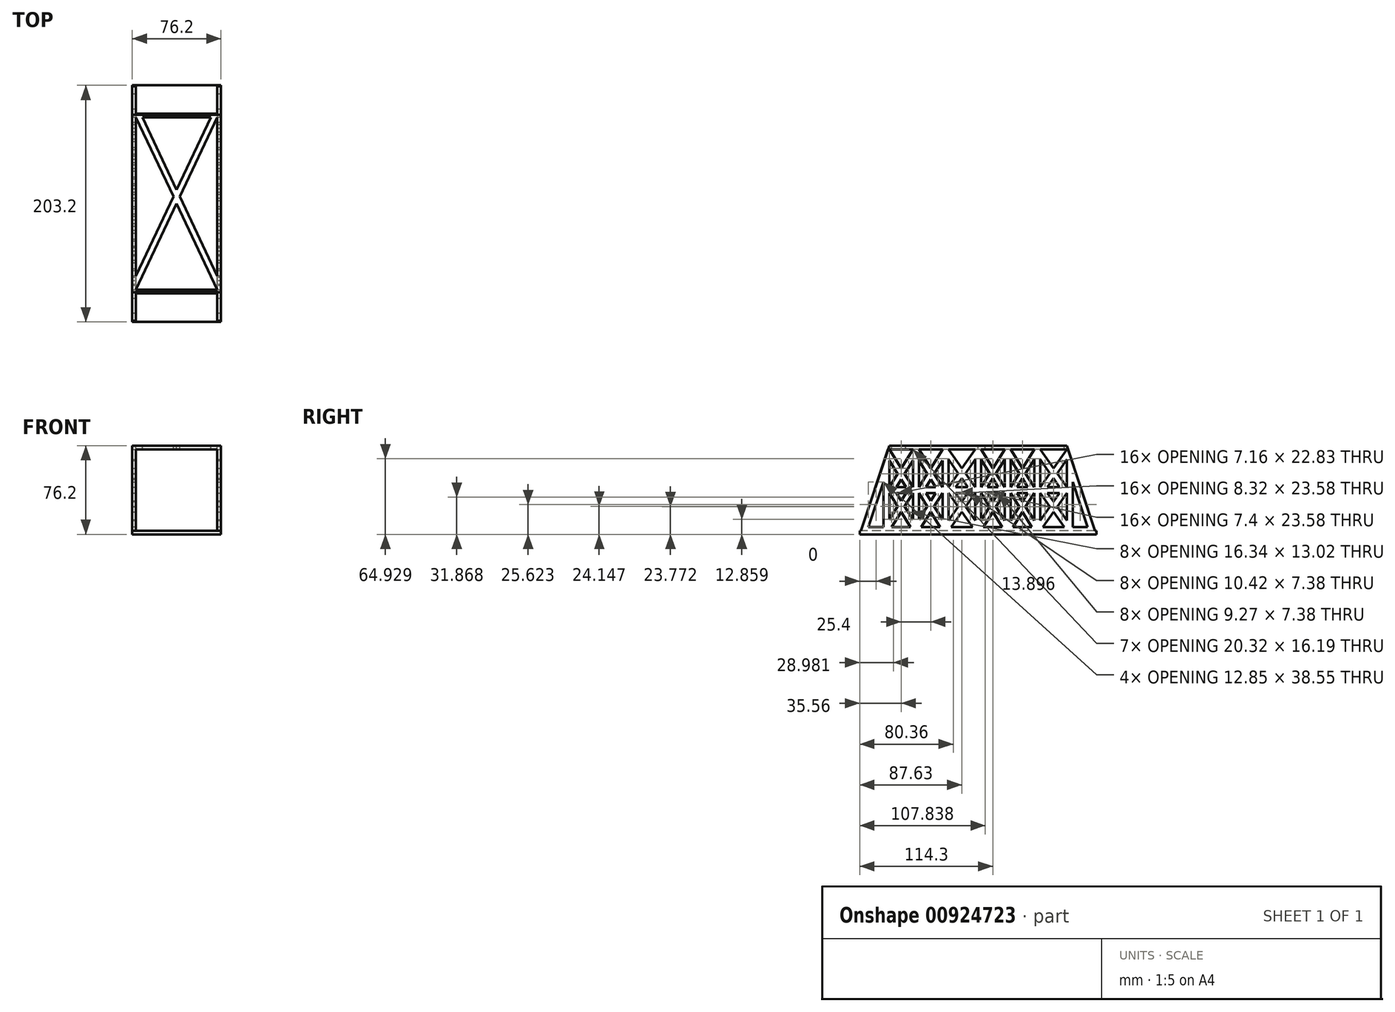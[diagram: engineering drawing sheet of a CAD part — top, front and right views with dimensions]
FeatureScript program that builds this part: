
annotation { "Feature Type Name" : "Feature", "Feature Type Description" : "" }
export const myFeature = defineFeature(function(context is Context, id is Id, definition is map)
    precondition{}
    {
        {
            var Q0;
            Q0=qCreatedBy(makeId("Right.planeOp"),FACE);
            var sketch = newSketch(context, id + "F0", { "sketchPlane" : qUnion([Q0])});
            skLineSegment(sketch, "E0", {"start": v(-101.6, -38.1) * mm, "end": v(101.6, -38.1) * mm});
            skLineSegment(sketch, "E1", {"start": v(-76.2, 38.1) * mm, "end": v(76.2, 38.1) * mm});
            skLineSegment(sketch, "E2", {"start": v(-76.2, 38.1) * mm, "end": v(-101.6, -38.1) * mm});
            skLineSegment(sketch, "E3", {"start": v(76.2, 38.1) * mm, "end": v(101.6, -38.1) * mm});
            skSolve(sketch);
        }
        {
            var Q0;
            Q0=qSketchRegion(id+"F0",true);
            extrude(context, id + "F1", {"entities" : qUnion([Q0]), "endBound" : BoundingType.SYMMETRIC, "depth" : 76.2 * mm, "offsetDistance" : 25.4 * mm});
        }
        {
            var Q0;
            Q0=makeQuery(id+"F1.opExtrude","CAP_FACE",FACE,{"disambiguationData":[OSD([sQuery(id+"F0.wireOp",EDGE,"E0"),sQuery(id+"F0.wireOp",EDGE,"E1"),sQuery(id+"F0.wireOp",EDGE,"E2"),sQuery(id+"F0.wireOp",EDGE,"E3")])],"isStart":false});
            var sketch = newSketch(context, id + "F2", { "sketchPlane" : qUnion([Q0])});
            skLineSegment(sketch, "E4.bottom", {"start": v(76.2, -34.93) * mm, "end": v(-76.2, -34.93) * mm});
            skLineSegment(sketch, "E4.top", {"start": v(76.2, 34.93) * mm, "end": v(-76.2, 34.93) * mm});
            skLineSegment(sketch, "E4.left", {"start": v(76.2, -34.93) * mm, "end": v(76.2, 34.93) * mm});
            skLineSegment(sketch, "E4.right", {"start": v(-76.2, -34.93) * mm, "end": v(-76.2, 34.93) * mm});
            skPoint(sketch, "E4.middle", {"position": v(0, 0) * mm});
            skLineSegment(sketch, "E5.bottom", {"start": v(76.2, -2.54) * mm, "end": v(-76.2, -2.54) * mm});
            skLineSegment(sketch, "E5.top", {"start": v(76.2, 2.54) * mm, "end": v(-76.2, 2.54) * mm});
            skLineSegment(sketch, "E5.left", {"start": v(76.2, -2.54) * mm, "end": v(76.2, 2.54) * mm});
            skLineSegment(sketch, "E5.right", {"start": v(-76.2, -2.54) * mm, "end": v(-76.2, 2.54) * mm});
            skLineSegment(sketch, "E6.bottom", {"start": v(-50.8, -34.93) * mm, "end": v(-55.88, -34.93) * mm});
            skLineSegment(sketch, "E6.top", {"start": v(-50.8, 34.93) * mm, "end": v(-55.88, 34.93) * mm});
            skLineSegment(sketch, "E6.left", {"start": v(-50.8, -34.92) * mm, "end": v(-50.8, 34.93) * mm});
            skLineSegment(sketch, "E6.right", {"start": v(-55.88, -34.92) * mm, "end": v(-55.88, 34.93) * mm});
            skPoint(sketch, "E6.middle", {"position": v(-53.34, 0) * mm});
            skLineSegment(sketch, "E7.bottom", {"start": v(-25.4, -34.93) * mm, "end": v(-30.48, -34.93) * mm});
            skLineSegment(sketch, "E7.top", {"start": v(-25.4, 34.93) * mm, "end": v(-30.48, 34.93) * mm});
            skLineSegment(sketch, "E7.left", {"start": v(-25.4, -34.93) * mm, "end": v(-25.4, 34.93) * mm});
            skLineSegment(sketch, "E7.right", {"start": v(-30.48, -34.93) * mm, "end": v(-30.48, 34.93) * mm});
            skPoint(sketch, "E7.middle", {"position": v(-27.94, 0) * mm});
            skLineSegment(sketch, "E8.bottom", {"start": v(27.94, -34.93) * mm, "end": v(22.86, -34.93) * mm});
            skLineSegment(sketch, "E8.top", {"start": v(27.94, 34.93) * mm, "end": v(22.86, 34.93) * mm});
            skLineSegment(sketch, "E8.left", {"start": v(27.94, -34.92) * mm, "end": v(27.94, 34.93) * mm});
            skLineSegment(sketch, "E8.right", {"start": v(22.86, -34.93) * mm, "end": v(22.86, 34.93) * mm});
            skPoint(sketch, "E8.middle", {"position": v(25.4, 0) * mm});
            skLineSegment(sketch, "E9.bottom", {"start": v(53.34, -34.93) * mm, "end": v(48.26, -34.93) * mm});
            skLineSegment(sketch, "E9.top", {"start": v(53.34, 34.93) * mm, "end": v(48.26, 34.93) * mm});
            skLineSegment(sketch, "E9.left", {"start": v(53.34, -34.93) * mm, "end": v(53.34, 34.93) * mm});
            skLineSegment(sketch, "E9.right", {"start": v(48.26, -34.93) * mm, "end": v(48.26, 34.93) * mm});
            skPoint(sketch, "E9.middle", {"position": v(50.8, 0) * mm});
            skLineSegment(sketch, "E10.bottom", {"start": v(2.54, -34.93) * mm, "end": v(-2.54, -34.93) * mm});
            skLineSegment(sketch, "E10.top", {"start": v(2.54, 34.93) * mm, "end": v(-2.54, 34.93) * mm});
            skLineSegment(sketch, "E10.left", {"start": v(2.54, -34.93) * mm, "end": v(2.54, 34.93) * mm});
            skLineSegment(sketch, "E10.right", {"start": v(-2.54, -34.93) * mm, "end": v(-2.54, 34.93) * mm});
            skLineSegment(sketch, "E11", {"start": v(-76.2, 34.93) * mm, "end": v(-55.88, 2.54) * mm});
            skLineSegment(sketch, "E12", {"start": v(-55.88, 34.93) * mm, "end": v(-76.2, 2.54) * mm});
            skLineSegment(sketch, "E13", {"start": v(-50.8, 34.93) * mm, "end": v(-30.48, 2.54) * mm});
            skLineSegment(sketch, "E14", {"start": v(-2.54, 34.92) * mm, "end": v(-25.4, 2.54) * mm});
            skLineSegment(sketch, "E15", {"start": v(-76.2, -2.54) * mm, "end": v(-55.88, -34.93) * mm});
            skLineSegment(sketch, "E16", {"start": v(-55.88, -2.54) * mm, "end": v(-76.2, -34.93) * mm});
            skLineSegment(sketch, "E17", {"start": v(-50.8, -2.54) * mm, "end": v(-30.48, -34.92) * mm});
            skLineSegment(sketch, "E18", {"start": v(-30.48, -2.54) * mm, "end": v(-50.8, -34.92) * mm});
            skLineSegment(sketch, "E19", {"start": v(-25.4, -2.54) * mm, "end": v(-2.54, -34.92) * mm});
            skLineSegment(sketch, "E20", {"start": v(-2.54, -2.54) * mm, "end": v(-25.4, -34.93) * mm});
            skLineSegment(sketch, "E21", {"start": v(-55.88, 25.37) * mm, "end": v(-70.2, 2.54) * mm});
            skLineSegment(sketch, "E22", {"start": v(-70.2, -2.54) * mm, "end": v(-55.88, -25.37) * mm});
            skLineSegment(sketch, "E23", {"start": v(-61.88, -2.54) * mm, "end": v(-76.2, -25.37) * mm});
            skLineSegment(sketch, "E24", {"start": v(-44.8, -2.54) * mm, "end": v(-30.48, -25.37) * mm});
            skLineSegment(sketch, "E25", {"start": v(-36.48, -2.54) * mm, "end": v(-50.8, -25.37) * mm});
            skLineSegment(sketch, "E26", {"start": v(-19.18, -2.54) * mm, "end": v(-2.54, -26.12) * mm});
            skLineSegment(sketch, "E27", {"start": v(-8.76, -2.54) * mm, "end": v(-25.4, -26.12) * mm});
            skLineSegment(sketch, "E28", {"start": v(-25.4, 34.93) * mm, "end": v(-2.54, 2.54) * mm});
            skLineSegment(sketch, "E29", {"start": v(-25.4, 26.12) * mm, "end": v(-8.76, 2.54) * mm});
            skLineSegment(sketch, "E30", {"start": v(-2.54, 26.12) * mm, "end": v(-19.18, 2.54) * mm});
            skLineSegment(sketch, "E31", {"start": v(-30.48, 34.92) * mm, "end": v(-50.8, 2.54) * mm});
            skLineSegment(sketch, "E32", {"start": v(-50.8, 25.37) * mm, "end": v(-36.48, 2.54) * mm});
            skLineSegment(sketch, "E33", {"start": v(-30.48, 25.37) * mm, "end": v(-44.8, 2.54) * mm});
            skLineSegment(sketch, "E34", {"start": v(-76.2, 25.37) * mm, "end": v(-61.88, 2.54) * mm});
            skLineSegment(sketch, "E35", {"start": v(2.54, 34.92) * mm, "end": v(22.86, 2.54) * mm});
            skLineSegment(sketch, "E36", {"start": v(22.86, 34.92) * mm, "end": v(2.54, 2.54) * mm});
            skLineSegment(sketch, "E37", {"start": v(2.54, 26.12) * mm, "end": v(17.33, 2.54) * mm});
            skLineSegment(sketch, "E38", {"start": v(22.86, 26.12) * mm, "end": v(8.07, 2.54) * mm});
            skLineSegment(sketch, "E39", {"start": v(27.94, 34.92) * mm, "end": v(48.26, 2.54) * mm});
            skLineSegment(sketch, "E40", {"start": v(27.94, 2.54) * mm, "end": v(48.26, 34.92) * mm});
            skLineSegment(sketch, "E41", {"start": v(53.34, 34.93) * mm, "end": v(76.2, 2.54) * mm});
            skLineSegment(sketch, "E42", {"start": v(53.34, 2.54) * mm, "end": v(76.2, 34.93) * mm});
            skLineSegment(sketch, "E43", {"start": v(53.34, -2.54) * mm, "end": v(76.2, -34.93) * mm});
            skLineSegment(sketch, "E44", {"start": v(53.34, -34.93) * mm, "end": v(76.2, -2.54) * mm});
            skLineSegment(sketch, "E45", {"start": v(48.26, -34.92) * mm, "end": v(27.94, -2.54) * mm});
            skLineSegment(sketch, "E46", {"start": v(48.26, -2.54) * mm, "end": v(27.94, -34.92) * mm});
            skLineSegment(sketch, "E47", {"start": v(2.54, -2.54) * mm, "end": v(22.86, -34.92) * mm});
            skLineSegment(sketch, "E48", {"start": v(22.86, -2.54) * mm, "end": v(2.54, -34.92) * mm});
            skLineSegment(sketch, "E49", {"start": v(27.94, 26.12) * mm, "end": v(42.73, 2.54) * mm});
            skLineSegment(sketch, "E50", {"start": v(48.26, 26.12) * mm, "end": v(33.47, 2.54) * mm});
            skLineSegment(sketch, "E51", {"start": v(53.34, 26.12) * mm, "end": v(69.98, 2.54) * mm});
            skLineSegment(sketch, "E52", {"start": v(76.2, 26.12) * mm, "end": v(59.56, 2.54) * mm});
            skLineSegment(sketch, "E53", {"start": v(59.56, -2.54) * mm, "end": v(76.2, -26.12) * mm});
            skLineSegment(sketch, "E54", {"start": v(69.98, -2.54) * mm, "end": v(53.34, -26.12) * mm});
            skLineSegment(sketch, "E55", {"start": v(48.26, -26.12) * mm, "end": v(33.47, -2.54) * mm});
            skLineSegment(sketch, "E56", {"start": v(42.73, -2.54) * mm, "end": v(27.94, -26.12) * mm});
            skLineSegment(sketch, "E57", {"start": v(22.86, -26.12) * mm, "end": v(8.07, -2.54) * mm});
            skLineSegment(sketch, "E58", {"start": v(17.33, -2.54) * mm, "end": v(2.54, -26.12) * mm});
            skLineSegment(sketch, "E59", {"start": v(-81.28, -34.93) * mm, "end": v(-81.28, 6.8) * mm});
            skLineSegment(sketch, "E60", {"start": v(-81.28, 6.8) * mm, "end": v(-95.19, -34.93) * mm});
            skLineSegment(sketch, "E61", {"start": v(-95.19, -34.92) * mm, "end": v(-81.28, -34.93) * mm});
            skLineSegment(sketch, "E62.MirrorCS", {"start": v(81.28, 6.8) * mm, "end": v(95.19, -34.93) * mm});
            skLineSegment(sketch, "E63.MirrorCS", {"start": v(81.28, -34.93) * mm, "end": v(81.28, 6.8) * mm});
            skLineSegment(sketch, "E64.MirrorCS", {"start": v(95.19, -34.92) * mm, "end": v(81.28, -34.93) * mm});
            skSolve(sketch);
        }
        {
            var Q0;
            Q0=makeQuery(id+"F2.imprint","IMPRINT",FACE,{"disambiguationData":[TD([[makeQuery(id+"F2.imprint","IMPRINT",EDGE,{"derivedFrom":sQuery(id+"F2.wireOp",EDGE,"E59")}),1.0]])]});
            var Q1;
            {var subQ0=sQuery(id+"F2.wireOp",EDGE,"E16");var subQ3=sQuery(id+"F2.wireOp",EDGE,"E15");var subQ5=makeQuery(id+"F2.imprint","INTERSECT",VERTEX,{"derivedFrom":[subQ3,subQ0]});Q1=makeQuery(id+"F2.imprint","IMPRINT",FACE,{"disambiguationData":[TD([[makeQuery(id+"F2.imprint","IMPRINT",EDGE,{"disambiguationData":[TD([[subQ5,-1.0]])],"derivedFrom":subQ0}),1.0]])]});}
            var Q2;
            {var subQ1=sQuery(id+"F2.wireOp",EDGE,"E4.right");var subQ3=sQuery(id+"F2.wireOp",EDGE,"E23");var subQ4=makeQuery(id+"F2.imprint","INTERSECT",VERTEX,{"derivedFrom":[subQ1,subQ3]});Q2=makeQuery(id+"F2.imprint","IMPRINT",FACE,{"disambiguationData":[TD([[makeQuery(id+"F2.imprint","IMPRINT",EDGE,{"disambiguationData":[TD([[subQ4,1.0]])],"derivedFrom":subQ3}),-1.0]])]});}
            var Q3;
            {var subQ0=sQuery(id+"F2.wireOp",EDGE,"E22");var subQ1=sQuery(id+"F2.wireOp",EDGE,"E5.bottom");var subQ2=makeQuery(id+"F2.imprint","INTERSECT",VERTEX,{"derivedFrom":[subQ1,subQ0]});Q3=makeQuery(id+"F2.imprint","IMPRINT",FACE,{"disambiguationData":[TD([[makeQuery(id+"F2.imprint","IMPRINT",EDGE,{"disambiguationData":[TD([[subQ2,1.0]])],"derivedFrom":subQ1}),1.0]])]});}
            var Q4;
            {var subQ1=sQuery(id+"F2.wireOp",EDGE,"E6.right");var subQ3=sQuery(id+"F2.wireOp",EDGE,"E22");var subQ4=makeQuery(id+"F2.imprint","INTERSECT",VERTEX,{"derivedFrom":[subQ1,subQ3]});Q4=makeQuery(id+"F2.imprint","IMPRINT",FACE,{"disambiguationData":[TD([[makeQuery(id+"F2.imprint","IMPRINT",EDGE,{"disambiguationData":[TD([[subQ4,1.0]])],"derivedFrom":subQ3}),1.0]])]});}
            var Q5;
            {var subQ0=sQuery(id+"F2.wireOp",EDGE,"E21");var subQ1=sQuery(id+"F2.wireOp",EDGE,"E5.top");var subQ2=makeQuery(id+"F2.imprint","INTERSECT",VERTEX,{"derivedFrom":[subQ1,subQ0]});Q5=makeQuery(id+"F2.imprint","IMPRINT",FACE,{"disambiguationData":[TD([[makeQuery(id+"F2.imprint","IMPRINT",EDGE,{"disambiguationData":[TD([[subQ2,1.0]])],"derivedFrom":subQ1}),-1.0]])]});}
            var Q6;
            {var subQ0=sQuery(id+"F2.wireOp",EDGE,"E11");var subQ3=sQuery(id+"F2.wireOp",EDGE,"E12");var subQ5=makeQuery(id+"F2.imprint","INTERSECT",VERTEX,{"derivedFrom":[subQ0,subQ3]});Q6=makeQuery(id+"F2.imprint","IMPRINT",FACE,{"disambiguationData":[TD([[makeQuery(id+"F2.imprint","IMPRINT",EDGE,{"disambiguationData":[TD([[subQ5,1.0]])],"derivedFrom":subQ0}),1.0]])]});}
            var Q7;
            {var subQ1=sQuery(id+"F2.wireOp",EDGE,"E4.right");var subQ3=sQuery(id+"F2.wireOp",EDGE,"E34");var subQ4=makeQuery(id+"F2.imprint","INTERSECT",VERTEX,{"derivedFrom":[subQ1,subQ3]});Q7=makeQuery(id+"F2.imprint","IMPRINT",FACE,{"disambiguationData":[TD([[makeQuery(id+"F2.imprint","IMPRINT",EDGE,{"disambiguationData":[TD([[subQ4,-1.0]])],"derivedFrom":subQ3}),-1.0]])]});}
            var Q8;
            {var subQ1=sQuery(id+"F2.wireOp",EDGE,"E6.right");var subQ3=sQuery(id+"F2.wireOp",EDGE,"E21");var subQ4=makeQuery(id+"F2.imprint","INTERSECT",VERTEX,{"derivedFrom":[subQ1,subQ3]});Q8=makeQuery(id+"F2.imprint","IMPRINT",FACE,{"disambiguationData":[TD([[makeQuery(id+"F2.imprint","IMPRINT",EDGE,{"disambiguationData":[TD([[subQ4,-1.0]])],"derivedFrom":subQ3}),1.0]])]});}
            var Q9;
            {var subQ0=sQuery(id+"F2.wireOp",EDGE,"E13");var subQ3=sQuery(id+"F2.wireOp",EDGE,"E31");var subQ5=makeQuery(id+"F2.imprint","INTERSECT",VERTEX,{"derivedFrom":[subQ0,subQ3]});Q9=makeQuery(id+"F2.imprint","IMPRINT",FACE,{"disambiguationData":[TD([[makeQuery(id+"F2.imprint","IMPRINT",EDGE,{"disambiguationData":[TD([[subQ5,1.0]])],"derivedFrom":subQ0}),1.0]])]});}
            var Q10;
            {var subQ1=sQuery(id+"F2.wireOp",EDGE,"E6.left");var subQ3=sQuery(id+"F2.wireOp",EDGE,"E32");var subQ4=makeQuery(id+"F2.imprint","INTERSECT",VERTEX,{"derivedFrom":[subQ1,subQ3]});Q10=makeQuery(id+"F2.imprint","IMPRINT",FACE,{"disambiguationData":[TD([[makeQuery(id+"F2.imprint","IMPRINT",EDGE,{"disambiguationData":[TD([[subQ4,-1.0]])],"derivedFrom":subQ3}),-1.0]])]});}
            var Q11;
            {var subQ1=sQuery(id+"F2.wireOp",EDGE,"E7.right");var subQ3=sQuery(id+"F2.wireOp",EDGE,"E33");var subQ4=makeQuery(id+"F2.imprint","INTERSECT",VERTEX,{"derivedFrom":[subQ1,subQ3]});Q11=makeQuery(id+"F2.imprint","IMPRINT",FACE,{"disambiguationData":[TD([[makeQuery(id+"F2.imprint","IMPRINT",EDGE,{"disambiguationData":[TD([[subQ4,-1.0]])],"derivedFrom":subQ3}),1.0]])]});}
            var Q12;
            {var subQ0=sQuery(id+"F2.wireOp",EDGE,"E32");var subQ1=sQuery(id+"F2.wireOp",EDGE,"E5.top");var subQ2=makeQuery(id+"F2.imprint","INTERSECT",VERTEX,{"derivedFrom":[subQ1,subQ0]});Q12=makeQuery(id+"F2.imprint","IMPRINT",FACE,{"disambiguationData":[TD([[makeQuery(id+"F2.imprint","IMPRINT",EDGE,{"disambiguationData":[TD([[subQ2,-1.0]])],"derivedFrom":subQ1}),-1.0]])]});}
            var Q13;
            {var subQ0=sQuery(id+"F2.wireOp",EDGE,"E24");var subQ1=sQuery(id+"F2.wireOp",EDGE,"E5.bottom");var subQ2=makeQuery(id+"F2.imprint","INTERSECT",VERTEX,{"derivedFrom":[subQ1,subQ0]});Q13=makeQuery(id+"F2.imprint","IMPRINT",FACE,{"disambiguationData":[TD([[makeQuery(id+"F2.imprint","IMPRINT",EDGE,{"disambiguationData":[TD([[subQ2,1.0]])],"derivedFrom":subQ1}),1.0]])]});}
            var Q14;
            {var subQ1=sQuery(id+"F2.wireOp",EDGE,"E6.left");var subQ3=sQuery(id+"F2.wireOp",EDGE,"E25");var subQ4=makeQuery(id+"F2.imprint","INTERSECT",VERTEX,{"derivedFrom":[subQ1,subQ3]});Q14=makeQuery(id+"F2.imprint","IMPRINT",FACE,{"disambiguationData":[TD([[makeQuery(id+"F2.imprint","IMPRINT",EDGE,{"disambiguationData":[TD([[subQ4,1.0]])],"derivedFrom":subQ3}),-1.0]])]});}
            var Q15;
            {var subQ1=sQuery(id+"F2.wireOp",EDGE,"E7.right");var subQ3=sQuery(id+"F2.wireOp",EDGE,"E24");var subQ4=makeQuery(id+"F2.imprint","INTERSECT",VERTEX,{"derivedFrom":[subQ1,subQ3]});Q15=makeQuery(id+"F2.imprint","IMPRINT",FACE,{"disambiguationData":[TD([[makeQuery(id+"F2.imprint","IMPRINT",EDGE,{"disambiguationData":[TD([[subQ4,1.0]])],"derivedFrom":subQ3}),1.0]])]});}
            var Q16;
            {var subQ0=sQuery(id+"F2.wireOp",EDGE,"E18");var subQ3=sQuery(id+"F2.wireOp",EDGE,"E17");var subQ5=makeQuery(id+"F2.imprint","INTERSECT",VERTEX,{"derivedFrom":[subQ3,subQ0]});Q16=makeQuery(id+"F2.imprint","IMPRINT",FACE,{"disambiguationData":[TD([[makeQuery(id+"F2.imprint","IMPRINT",EDGE,{"disambiguationData":[TD([[subQ5,-1.0]])],"derivedFrom":subQ3}),-1.0]])]});}
            var Q17;
            {var subQ1=sQuery(id+"F2.wireOp",EDGE,"E7.left");var subQ3=sQuery(id+"F2.wireOp",EDGE,"E29");var subQ4=makeQuery(id+"F2.imprint","INTERSECT",VERTEX,{"derivedFrom":[subQ1,subQ3]});Q17=makeQuery(id+"F2.imprint","IMPRINT",FACE,{"disambiguationData":[TD([[makeQuery(id+"F2.imprint","IMPRINT",EDGE,{"disambiguationData":[TD([[subQ4,-1.0]])],"derivedFrom":subQ3}),-1.0]])]});}
            var Q18;
            {var subQ0=sQuery(id+"F2.wireOp",EDGE,"E28");var subQ3=sQuery(id+"F2.wireOp",EDGE,"E14");var subQ5=makeQuery(id+"F2.imprint","INTERSECT",VERTEX,{"derivedFrom":[subQ3,subQ0]});Q18=makeQuery(id+"F2.imprint","IMPRINT",FACE,{"disambiguationData":[TD([[makeQuery(id+"F2.imprint","IMPRINT",EDGE,{"disambiguationData":[TD([[subQ5,1.0]])],"derivedFrom":subQ3}),-1.0]])]});}
            var Q19;
            {var subQ1=sQuery(id+"F2.wireOp",EDGE,"E10.right");var subQ3=sQuery(id+"F2.wireOp",EDGE,"E30");var subQ4=makeQuery(id+"F2.imprint","INTERSECT",VERTEX,{"derivedFrom":[subQ1,subQ3]});Q19=makeQuery(id+"F2.imprint","IMPRINT",FACE,{"disambiguationData":[TD([[makeQuery(id+"F2.imprint","IMPRINT",EDGE,{"disambiguationData":[TD([[subQ4,-1.0]])],"derivedFrom":subQ3}),1.0]])]});}
            var Q20;
            {var subQ0=sQuery(id+"F2.wireOp",EDGE,"E29");var subQ1=sQuery(id+"F2.wireOp",EDGE,"E5.top");var subQ2=makeQuery(id+"F2.imprint","INTERSECT",VERTEX,{"derivedFrom":[subQ1,subQ0]});Q20=makeQuery(id+"F2.imprint","IMPRINT",FACE,{"disambiguationData":[TD([[makeQuery(id+"F2.imprint","IMPRINT",EDGE,{"disambiguationData":[TD([[subQ2,-1.0]])],"derivedFrom":subQ1}),-1.0]])]});}
            var Q21;
            {var subQ0=sQuery(id+"F2.wireOp",EDGE,"E26");var subQ1=sQuery(id+"F2.wireOp",EDGE,"E5.bottom");var subQ2=makeQuery(id+"F2.imprint","INTERSECT",VERTEX,{"derivedFrom":[subQ1,subQ0]});Q21=makeQuery(id+"F2.imprint","IMPRINT",FACE,{"disambiguationData":[TD([[makeQuery(id+"F2.imprint","IMPRINT",EDGE,{"disambiguationData":[TD([[subQ2,1.0]])],"derivedFrom":subQ1}),1.0]])]});}
            var Q22;
            {var subQ1=sQuery(id+"F2.wireOp",EDGE,"E7.left");var subQ3=sQuery(id+"F2.wireOp",EDGE,"E27");var subQ4=makeQuery(id+"F2.imprint","INTERSECT",VERTEX,{"derivedFrom":[subQ1,subQ3]});Q22=makeQuery(id+"F2.imprint","IMPRINT",FACE,{"disambiguationData":[TD([[makeQuery(id+"F2.imprint","IMPRINT",EDGE,{"disambiguationData":[TD([[subQ4,1.0]])],"derivedFrom":subQ3}),-1.0]])]});}
            var Q23;
            {var subQ1=sQuery(id+"F2.wireOp",EDGE,"E10.right");var subQ3=sQuery(id+"F2.wireOp",EDGE,"E26");var subQ4=makeQuery(id+"F2.imprint","INTERSECT",VERTEX,{"derivedFrom":[subQ1,subQ3]});Q23=makeQuery(id+"F2.imprint","IMPRINT",FACE,{"disambiguationData":[TD([[makeQuery(id+"F2.imprint","IMPRINT",EDGE,{"disambiguationData":[TD([[subQ4,1.0]])],"derivedFrom":subQ3}),1.0]])]});}
            var Q24;
            {var subQ0=sQuery(id+"F2.wireOp",EDGE,"E20");var subQ3=sQuery(id+"F2.wireOp",EDGE,"E19");var subQ5=makeQuery(id+"F2.imprint","INTERSECT",VERTEX,{"derivedFrom":[subQ3,subQ0]});Q24=makeQuery(id+"F2.imprint","IMPRINT",FACE,{"disambiguationData":[TD([[makeQuery(id+"F2.imprint","IMPRINT",EDGE,{"disambiguationData":[TD([[subQ5,-1.0]])],"derivedFrom":subQ3}),-1.0]])]});}
            var Q25;
            {var subQ1=sQuery(id+"F2.wireOp",EDGE,"E10.left");var subQ3=sQuery(id+"F2.wireOp",EDGE,"E37");var subQ4=makeQuery(id+"F2.imprint","INTERSECT",VERTEX,{"derivedFrom":[subQ1,subQ3]});Q25=makeQuery(id+"F2.imprint","IMPRINT",FACE,{"disambiguationData":[TD([[makeQuery(id+"F2.imprint","IMPRINT",EDGE,{"disambiguationData":[TD([[subQ4,-1.0]])],"derivedFrom":subQ3}),-1.0]])]});}
            var Q26;
            {var subQ0=sQuery(id+"F2.wireOp",EDGE,"E36");var subQ3=sQuery(id+"F2.wireOp",EDGE,"E35");var subQ5=makeQuery(id+"F2.imprint","INTERSECT",VERTEX,{"derivedFrom":[subQ3,subQ0]});Q26=makeQuery(id+"F2.imprint","IMPRINT",FACE,{"disambiguationData":[TD([[makeQuery(id+"F2.imprint","IMPRINT",EDGE,{"disambiguationData":[TD([[subQ5,1.0]])],"derivedFrom":subQ3}),1.0]])]});}
            var Q27;
            {var subQ1=sQuery(id+"F2.wireOp",EDGE,"E8.right");var subQ3=sQuery(id+"F2.wireOp",EDGE,"E38");var subQ4=makeQuery(id+"F2.imprint","INTERSECT",VERTEX,{"derivedFrom":[subQ1,subQ3]});Q27=makeQuery(id+"F2.imprint","IMPRINT",FACE,{"disambiguationData":[TD([[makeQuery(id+"F2.imprint","IMPRINT",EDGE,{"disambiguationData":[TD([[subQ4,-1.0]])],"derivedFrom":subQ3}),1.0]])]});}
            var Q28;
            {var subQ0=sQuery(id+"F2.wireOp",EDGE,"E37");var subQ1=sQuery(id+"F2.wireOp",EDGE,"E5.top");var subQ2=makeQuery(id+"F2.imprint","INTERSECT",VERTEX,{"derivedFrom":[subQ1,subQ0]});Q28=makeQuery(id+"F2.imprint","IMPRINT",FACE,{"disambiguationData":[TD([[makeQuery(id+"F2.imprint","IMPRINT",EDGE,{"disambiguationData":[TD([[subQ2,-1.0]])],"derivedFrom":subQ1}),-1.0]])]});}
            var Q29;
            {var subQ0=sQuery(id+"F2.wireOp",EDGE,"E57");var subQ1=sQuery(id+"F2.wireOp",EDGE,"E5.bottom");var subQ2=makeQuery(id+"F2.imprint","INTERSECT",VERTEX,{"derivedFrom":[subQ1,subQ0]});Q29=makeQuery(id+"F2.imprint","IMPRINT",FACE,{"disambiguationData":[TD([[makeQuery(id+"F2.imprint","IMPRINT",EDGE,{"disambiguationData":[TD([[subQ2,1.0]])],"derivedFrom":subQ1}),1.0]])]});}
            var Q30;
            {var subQ1=sQuery(id+"F2.wireOp",EDGE,"E10.left");var subQ3=sQuery(id+"F2.wireOp",EDGE,"E58");var subQ4=makeQuery(id+"F2.imprint","INTERSECT",VERTEX,{"derivedFrom":[subQ1,subQ3]});Q30=makeQuery(id+"F2.imprint","IMPRINT",FACE,{"disambiguationData":[TD([[makeQuery(id+"F2.imprint","IMPRINT",EDGE,{"disambiguationData":[TD([[subQ4,1.0]])],"derivedFrom":subQ3}),-1.0]])]});}
            var Q31;
            {var subQ1=sQuery(id+"F2.wireOp",EDGE,"E8.right");var subQ3=sQuery(id+"F2.wireOp",EDGE,"E57");var subQ4=makeQuery(id+"F2.imprint","INTERSECT",VERTEX,{"derivedFrom":[subQ1,subQ3]});Q31=makeQuery(id+"F2.imprint","IMPRINT",FACE,{"disambiguationData":[TD([[makeQuery(id+"F2.imprint","IMPRINT",EDGE,{"disambiguationData":[TD([[subQ4,-1.0]])],"derivedFrom":subQ3}),-1.0]])]});}
            var Q32;
            {var subQ0=sQuery(id+"F2.wireOp",EDGE,"E47");var subQ3=sQuery(id+"F2.wireOp",EDGE,"E48");var subQ5=makeQuery(id+"F2.imprint","INTERSECT",VERTEX,{"derivedFrom":[subQ0,subQ3]});Q32=makeQuery(id+"F2.imprint","IMPRINT",FACE,{"disambiguationData":[TD([[makeQuery(id+"F2.imprint","IMPRINT",EDGE,{"disambiguationData":[TD([[subQ5,-1.0]])],"derivedFrom":subQ0}),-1.0]])]});}
            var Q33;
            {var subQ1=sQuery(id+"F2.wireOp",EDGE,"E8.left");var subQ3=sQuery(id+"F2.wireOp",EDGE,"E49");var subQ4=makeQuery(id+"F2.imprint","INTERSECT",VERTEX,{"derivedFrom":[subQ1,subQ3]});Q33=makeQuery(id+"F2.imprint","IMPRINT",FACE,{"disambiguationData":[TD([[makeQuery(id+"F2.imprint","IMPRINT",EDGE,{"disambiguationData":[TD([[subQ4,-1.0]])],"derivedFrom":subQ3}),-1.0]])]});}
            var Q34;
            {var subQ0=sQuery(id+"F2.wireOp",EDGE,"E39");var subQ3=sQuery(id+"F2.wireOp",EDGE,"E40");var subQ5=makeQuery(id+"F2.imprint","INTERSECT",VERTEX,{"derivedFrom":[subQ0,subQ3]});Q34=makeQuery(id+"F2.imprint","IMPRINT",FACE,{"disambiguationData":[TD([[makeQuery(id+"F2.imprint","IMPRINT",EDGE,{"disambiguationData":[TD([[subQ5,1.0]])],"derivedFrom":subQ0}),1.0]])]});}
            var Q35;
            {var subQ1=sQuery(id+"F2.wireOp",EDGE,"E9.right");var subQ3=sQuery(id+"F2.wireOp",EDGE,"E50");var subQ4=makeQuery(id+"F2.imprint","INTERSECT",VERTEX,{"derivedFrom":[subQ1,subQ3]});Q35=makeQuery(id+"F2.imprint","IMPRINT",FACE,{"disambiguationData":[TD([[makeQuery(id+"F2.imprint","IMPRINT",EDGE,{"disambiguationData":[TD([[subQ4,-1.0]])],"derivedFrom":subQ3}),1.0]])]});}
            var Q36;
            {var subQ0=sQuery(id+"F2.wireOp",EDGE,"E49");var subQ1=sQuery(id+"F2.wireOp",EDGE,"E5.top");var subQ2=makeQuery(id+"F2.imprint","INTERSECT",VERTEX,{"derivedFrom":[subQ1,subQ0]});Q36=makeQuery(id+"F2.imprint","IMPRINT",FACE,{"disambiguationData":[TD([[makeQuery(id+"F2.imprint","IMPRINT",EDGE,{"disambiguationData":[TD([[subQ2,-1.0]])],"derivedFrom":subQ1}),-1.0]])]});}
            var Q37;
            {var subQ0=sQuery(id+"F2.wireOp",EDGE,"E55");var subQ1=sQuery(id+"F2.wireOp",EDGE,"E5.bottom");var subQ2=makeQuery(id+"F2.imprint","INTERSECT",VERTEX,{"derivedFrom":[subQ1,subQ0]});Q37=makeQuery(id+"F2.imprint","IMPRINT",FACE,{"disambiguationData":[TD([[makeQuery(id+"F2.imprint","IMPRINT",EDGE,{"disambiguationData":[TD([[subQ2,1.0]])],"derivedFrom":subQ1}),1.0]])]});}
            var Q38;
            {var subQ1=sQuery(id+"F2.wireOp",EDGE,"E8.left");var subQ3=sQuery(id+"F2.wireOp",EDGE,"E56");var subQ4=makeQuery(id+"F2.imprint","INTERSECT",VERTEX,{"derivedFrom":[subQ1,subQ3]});Q38=makeQuery(id+"F2.imprint","IMPRINT",FACE,{"disambiguationData":[TD([[makeQuery(id+"F2.imprint","IMPRINT",EDGE,{"disambiguationData":[TD([[subQ4,1.0]])],"derivedFrom":subQ3}),-1.0]])]});}
            var Q39;
            {var subQ1=sQuery(id+"F2.wireOp",EDGE,"E9.right");var subQ3=sQuery(id+"F2.wireOp",EDGE,"E55");var subQ4=makeQuery(id+"F2.imprint","INTERSECT",VERTEX,{"derivedFrom":[subQ1,subQ3]});Q39=makeQuery(id+"F2.imprint","IMPRINT",FACE,{"disambiguationData":[TD([[makeQuery(id+"F2.imprint","IMPRINT",EDGE,{"disambiguationData":[TD([[subQ4,-1.0]])],"derivedFrom":subQ3}),-1.0]])]});}
            var Q40;
            {var subQ0=sQuery(id+"F2.wireOp",EDGE,"E46");var subQ3=sQuery(id+"F2.wireOp",EDGE,"E45");var subQ5=makeQuery(id+"F2.imprint","INTERSECT",VERTEX,{"derivedFrom":[subQ3,subQ0]});Q40=makeQuery(id+"F2.imprint","IMPRINT",FACE,{"disambiguationData":[TD([[makeQuery(id+"F2.imprint","IMPRINT",EDGE,{"disambiguationData":[TD([[subQ5,1.0]])],"derivedFrom":subQ3}),1.0]])]});}
            var Q41;
            {var subQ1=sQuery(id+"F2.wireOp",EDGE,"E9.left");var subQ3=sQuery(id+"F2.wireOp",EDGE,"E51");var subQ4=makeQuery(id+"F2.imprint","INTERSECT",VERTEX,{"derivedFrom":[subQ1,subQ3]});Q41=makeQuery(id+"F2.imprint","IMPRINT",FACE,{"disambiguationData":[TD([[makeQuery(id+"F2.imprint","IMPRINT",EDGE,{"disambiguationData":[TD([[subQ4,-1.0]])],"derivedFrom":subQ3}),-1.0]])]});}
            var Q42;
            {var subQ0=sQuery(id+"F2.wireOp",EDGE,"E42");var subQ3=sQuery(id+"F2.wireOp",EDGE,"E41");var subQ5=makeQuery(id+"F2.imprint","INTERSECT",VERTEX,{"derivedFrom":[subQ3,subQ0]});Q42=makeQuery(id+"F2.imprint","IMPRINT",FACE,{"disambiguationData":[TD([[makeQuery(id+"F2.imprint","IMPRINT",EDGE,{"disambiguationData":[TD([[subQ5,-1.0]])],"derivedFrom":subQ0}),1.0]])]});}
            var Q43;
            {var subQ1=sQuery(id+"F2.wireOp",EDGE,"E4.left");var subQ3=sQuery(id+"F2.wireOp",EDGE,"E52");var subQ4=makeQuery(id+"F2.imprint","INTERSECT",VERTEX,{"derivedFrom":[subQ1,subQ3]});Q43=makeQuery(id+"F2.imprint","IMPRINT",FACE,{"disambiguationData":[TD([[makeQuery(id+"F2.imprint","IMPRINT",EDGE,{"disambiguationData":[TD([[subQ4,-1.0]])],"derivedFrom":subQ3}),1.0]])]});}
            var Q44;
            {var subQ0=sQuery(id+"F2.wireOp",EDGE,"E51");var subQ1=sQuery(id+"F2.wireOp",EDGE,"E5.top");var subQ2=makeQuery(id+"F2.imprint","INTERSECT",VERTEX,{"derivedFrom":[subQ1,subQ0]});Q44=makeQuery(id+"F2.imprint","IMPRINT",FACE,{"disambiguationData":[TD([[makeQuery(id+"F2.imprint","IMPRINT",EDGE,{"disambiguationData":[TD([[subQ2,-1.0]])],"derivedFrom":subQ1}),-1.0]])]});}
            var Q45;
            {var subQ0=sQuery(id+"F2.wireOp",EDGE,"E53");var subQ1=sQuery(id+"F2.wireOp",EDGE,"E5.bottom");var subQ2=makeQuery(id+"F2.imprint","INTERSECT",VERTEX,{"derivedFrom":[subQ1,subQ0]});Q45=makeQuery(id+"F2.imprint","IMPRINT",FACE,{"disambiguationData":[TD([[makeQuery(id+"F2.imprint","IMPRINT",EDGE,{"disambiguationData":[TD([[subQ2,1.0]])],"derivedFrom":subQ1}),1.0]])]});}
            var Q46;
            {var subQ1=sQuery(id+"F2.wireOp",EDGE,"E9.left");var subQ3=sQuery(id+"F2.wireOp",EDGE,"E54");var subQ4=makeQuery(id+"F2.imprint","INTERSECT",VERTEX,{"derivedFrom":[subQ1,subQ3]});Q46=makeQuery(id+"F2.imprint","IMPRINT",FACE,{"disambiguationData":[TD([[makeQuery(id+"F2.imprint","IMPRINT",EDGE,{"disambiguationData":[TD([[subQ4,1.0]])],"derivedFrom":subQ3}),-1.0]])]});}
            var Q47;
            {var subQ0=sQuery(id+"F2.wireOp",EDGE,"E43");var subQ3=sQuery(id+"F2.wireOp",EDGE,"E44");var subQ5=makeQuery(id+"F2.imprint","INTERSECT",VERTEX,{"derivedFrom":[subQ0,subQ3]});Q47=makeQuery(id+"F2.imprint","IMPRINT",FACE,{"disambiguationData":[TD([[makeQuery(id+"F2.imprint","IMPRINT",EDGE,{"disambiguationData":[TD([[subQ5,-1.0]])],"derivedFrom":subQ0}),-1.0]])]});}
            var Q48;
            {var subQ1=sQuery(id+"F2.wireOp",EDGE,"E4.left");var subQ3=sQuery(id+"F2.wireOp",EDGE,"E53");var subQ4=makeQuery(id+"F2.imprint","INTERSECT",VERTEX,{"derivedFrom":[subQ1,subQ3]});Q48=makeQuery(id+"F2.imprint","IMPRINT",FACE,{"disambiguationData":[TD([[makeQuery(id+"F2.imprint","IMPRINT",EDGE,{"disambiguationData":[TD([[subQ4,1.0]])],"derivedFrom":subQ3}),1.0]])]});}
            var Q49;
            Q49=makeQuery(id+"F2.imprint","IMPRINT",FACE,{"disambiguationData":[TD([[makeQuery(id+"F2.imprint","IMPRINT",EDGE,{"derivedFrom":sQuery(id+"F2.wireOp",EDGE,"E62.MirrorCS")}),-1.0]])]});
            extrude(context, id + "F3", {"entities" : qUnion([Q0, Q1, Q2, Q3, Q4, Q5, Q6, Q7, Q8, Q9, Q10, Q11, Q12, Q13, Q14, Q15, Q16, Q17, Q18, Q19, Q20, Q21, Q22, Q23, Q24, Q25, Q26, Q27, Q28, Q29, Q30, Q31, Q32, Q33, Q34, Q35, Q36, Q37, Q38, Q39, Q40, Q41, Q42, Q43, Q44, Q45, Q46, Q47, Q48, Q49]), "operationType" : NewBodyOperationType.REMOVE, "oppositeDirection" : true, "depth" : 76.2 * mm, "offsetDistance" : 25.4 * mm});
        }
        {
            var Q0;
            Q0=qCreatedBy(makeId("Front.planeOp"),FACE);
            var sketch = newSketch(context, id + "F4", { "sketchPlane" : qUnion([Q0])});
            skLineSegment(sketch, "E65.bottom", {"start": v(34.92, -34.93) * mm, "end": v(-34.92, -34.93) * mm});
            skLineSegment(sketch, "E65.top", {"start": v(34.92, 34.93) * mm, "end": v(-34.92, 34.93) * mm});
            skLineSegment(sketch, "E65.left", {"start": v(34.92, -34.93) * mm, "end": v(34.92, 34.93) * mm});
            skLineSegment(sketch, "E65.right", {"start": v(-34.92, -34.93) * mm, "end": v(-34.92, 34.93) * mm});
            skPoint(sketch, "E65.middle", {"position": v(0, 0) * mm});
            skSolve(sketch);
        }
        {
            var Q0;
            Q0=qSketchRegion(id+"F4",true);
            extrude(context, id + "F5", {"entities" : qUnion([Q0]), "operationType" : NewBodyOperationType.REMOVE, "endBound" : BoundingType.SYMMETRIC, "oppositeDirection" : true, "depth" : 254 * mm, "offsetDistance" : 25.4 * mm});
        }
        {
            var Q0;
            Q0=makeQuery(id+"F1.opExtrude","SWEPT_FACE",FACE,{"disambiguationData":[OSD([sQuery(id+"F0.wireOp",EDGE,"E1")])]});
            var sketch = newSketch(context, id + "F6", { "sketchPlane" : qUnion([Q0])});
            skLineSegment(sketch, "E66.bottom", {"start": v(34.93, -74.08) * mm, "end": v(-34.93, -74.08) * mm});
            skLineSegment(sketch, "E66.top", {"start": v(34.93, 74.08) * mm, "end": v(-34.93, 74.08) * mm});
            skLineSegment(sketch, "E66.left", {"start": v(34.93, -74.08) * mm, "end": v(34.93, 74.08) * mm});
            skLineSegment(sketch, "E66.right", {"start": v(-34.93, -74.08) * mm, "end": v(-34.93, 74.08) * mm});
            skPoint(sketch, "E66.middle", {"position": v(0, 0) * mm});
            skLineSegment(sketch, "E67", {"start": v(-34.93, 74.08) * mm, "end": v(34.93, -74.08) * mm});
            skLineSegment(sketch, "E68", {"start": v(34.92, 74.08) * mm, "end": v(-34.92, -74.08) * mm});
            skLineSegment(sketch, "E69", {"start": v(-29.3, 74.08) * mm, "end": v(34.93, -62.17) * mm});
            skLineSegment(sketch, "E70", {"start": v(29.3, 74.08) * mm, "end": v(-34.93, -62.17) * mm});
            skSolve(sketch);
        }
        {
            var Q0;
            {var subQ1=sQuery(id+"F6.wireOp",EDGE,"E66.right");var subQ3=sQuery(id+"F6.wireOp",EDGE,"E70");var subQ4=makeQuery(id+"F6.imprint","INTERSECT",VERTEX,{"derivedFrom":[subQ1,subQ3]});Q0=makeQuery(id+"F6.imprint","IMPRINT",FACE,{"disambiguationData":[TD([[makeQuery(id+"F6.imprint","IMPRINT",EDGE,{"disambiguationData":[TD([[subQ4,1.0]])],"derivedFrom":subQ3}),-1.0]])]});}
            var Q1;
            {var subQ0=sQuery(id+"F6.wireOp",EDGE,"E69");var subQ1=sQuery(id+"F6.wireOp",EDGE,"E66.top");var subQ2=makeQuery(id+"F6.imprint","INTERSECT",VERTEX,{"derivedFrom":[subQ1,subQ0]});Q1=makeQuery(id+"F6.imprint","IMPRINT",FACE,{"disambiguationData":[TD([[makeQuery(id+"F6.imprint","IMPRINT",EDGE,{"disambiguationData":[TD([[subQ2,1.0]])],"derivedFrom":subQ1}),1.0]])]});}
            var Q2;
            {var subQ1=sQuery(id+"F6.wireOp",EDGE,"E66.left");var subQ3=sQuery(id+"F6.wireOp",EDGE,"E69");var subQ4=makeQuery(id+"F6.imprint","INTERSECT",VERTEX,{"derivedFrom":[subQ1,subQ3]});Q2=makeQuery(id+"F6.imprint","IMPRINT",FACE,{"disambiguationData":[TD([[makeQuery(id+"F6.imprint","IMPRINT",EDGE,{"disambiguationData":[TD([[subQ4,1.0]])],"derivedFrom":subQ3}),1.0]])]});}
            var Q3;
            {var subQ0=sQuery(id+"F6.wireOp",EDGE,"E66.bottom");Q3=makeQuery(id+"F6.imprint","IMPRINT",FACE,{"disambiguationData":[TD([[makeQuery(id+"F6.imprint","IMPRINT",EDGE,{"derivedFrom":subQ0}),-1.0]])]});}
            extrude(context, id + "F7", {"entities" : qUnion([Q0, Q1, Q2, Q3]), "operationType" : NewBodyOperationType.REMOVE, "oppositeDirection" : true, "depth" : 3.17 * mm, "offsetDistance" : 25.4 * mm});
        }
        {
            var Q0;
            Q0=makeQuery(id+"F1.opExtrude","CAP_FACE",FACE,{"disambiguationData":[OSD([sQuery(id+"F0.wireOp",EDGE,"E0"),sQuery(id+"F0.wireOp",EDGE,"E1"),sQuery(id+"F0.wireOp",EDGE,"E2"),sQuery(id+"F0.wireOp",EDGE,"E3")])],"isStart":false});
            var sketch = newSketch(context, id + "F8", { "sketchPlane" : qUnion([Q0])});
            skLineSegment(sketch, "E71.bottom", {"start": v(-101.6, -38.1) * mm, "end": v(-95.19, -38.1) * mm});
            skLineSegment(sketch, "E71.top", {"start": v(-101.6, -34.93) * mm, "end": v(-95.19, -34.93) * mm});
            skLineSegment(sketch, "E71.left", {"start": v(-101.6, -38.1) * mm, "end": v(-101.6, -34.93) * mm});
            skLineSegment(sketch, "E71.right", {"start": v(-95.19, -38.1) * mm, "end": v(-95.19, -34.93) * mm});
            skLineSegment(sketch, "E72.MirrorCS", {"start": v(101.6, -38.1) * mm, "end": v(95.19, -38.1) * mm});
            skLineSegment(sketch, "E73.MirrorCS", {"start": v(101.6, -34.93) * mm, "end": v(95.19, -34.93) * mm});
            skLineSegment(sketch, "E74.MirrorCS", {"start": v(101.6, -38.1) * mm, "end": v(101.6, -34.93) * mm});
            skLineSegment(sketch, "E75.MirrorCS", {"start": v(95.19, -38.1) * mm, "end": v(95.19, -34.93) * mm});
            skSolve(sketch);
        }
        {
            var Q0;
            Q0=qSketchRegion(id+"F8",true);
            extrude(context, id + "F9", {"entities" : qUnion([Q0]), "operationType" : NewBodyOperationType.ADD, "oppositeDirection" : true, "depth" : 76.2 * mm, "offsetDistance" : 25.4 * mm});
        }
        {
            var Q0;
            {var subQ0=sQuery(id+"F2.wireOp",EDGE,"E4.bottom");var subQ1=sQuery(id+"F2.wireOp",EDGE,"E6.bottom");var subQ2=sQuery(id+"F2.wireOp",EDGE,"E7.bottom");var subQ4=sQuery(id+"F2.wireOp",EDGE,"E8.bottom");Q0=makeQuery(id+"F9.boolean.opBoolean","MERGE",FACE,{"derivedFrom":[makeQuery(id+"F5.boolean.opBoolean","MERGE",FACE,{"derivedFrom":[makeQuery(id+"F3.boolean.opBoolean","COPY",FACE,{"derivedFrom":makeQuery(id+"F3.opExtrude","SWEPT_FACE",FACE,{"disambiguationData":[OSD([subQ0]),TDD([makeQuery(id+"F2.imprint","IMPRINT",EDGE,{"disambiguationData":[TD([[makeQuery(id+"F2.imprint","INTERSECT",VERTEX,{"derivedFrom":[subQ0,sQuery(id+"F2.wireOp",EDGE,"E4.left"),sQuery(id+"F2.wireOp",EDGE,"E43")]}),-1.0]])],"derivedFrom":subQ0})])]})}),makeQuery(id+"F3.boolean.opBoolean","COPY",FACE,{"derivedFrom":makeQuery(id+"F3.opExtrude","SWEPT_FACE",FACE,{"disambiguationData":[OSD([subQ0]),TDD([makeQuery(id+"F2.imprint","IMPRINT",EDGE,{"disambiguationData":[TD([[makeQuery(id+"F2.imprint","INTERSECT",VERTEX,{"derivedFrom":[subQ0,subQ4,sQuery(id+"F2.wireOp",EDGE,"E8.left"),sQuery(id+"F2.wireOp",EDGE,"E46")]}),1.0]])],"derivedFrom":subQ0})])]})}),makeQuery(id+"F3.boolean.opBoolean","COPY",FACE,{"derivedFrom":makeQuery(id+"F3.opExtrude","SWEPT_FACE",FACE,{"disambiguationData":[OSD([subQ0]),TDD([makeQuery(id+"F2.imprint","IMPRINT",EDGE,{"disambiguationData":[TD([[makeQuery(id+"F2.imprint","INTERSECT",VERTEX,{"derivedFrom":[subQ0,subQ4,sQuery(id+"F2.wireOp",EDGE,"E8.right"),sQuery(id+"F2.wireOp",EDGE,"E47")]}),-1.0]])],"derivedFrom":subQ0})])]})}),makeQuery(id+"F3.boolean.opBoolean","COPY",FACE,{"derivedFrom":makeQuery(id+"F3.opExtrude","SWEPT_FACE",FACE,{"disambiguationData":[OSD([subQ0]),TDD([makeQuery(id+"F2.imprint","IMPRINT",EDGE,{"disambiguationData":[TD([[makeQuery(id+"F2.imprint","INTERSECT",VERTEX,{"derivedFrom":[subQ0,subQ2,sQuery(id+"F2.wireOp",EDGE,"E7.left"),sQuery(id+"F2.wireOp",EDGE,"E20")]}),1.0]])],"derivedFrom":subQ0})])]})}),makeQuery(id+"F3.boolean.opBoolean","COPY",FACE,{"derivedFrom":makeQuery(id+"F3.opExtrude","SWEPT_FACE",FACE,{"disambiguationData":[OSD([subQ0]),TDD([makeQuery(id+"F2.imprint","IMPRINT",EDGE,{"disambiguationData":[TD([[makeQuery(id+"F2.imprint","INTERSECT",VERTEX,{"derivedFrom":[subQ0,subQ1,sQuery(id+"F2.wireOp",EDGE,"E6.left"),sQuery(id+"F2.wireOp",EDGE,"E18")]}),1.0]])],"derivedFrom":subQ0})])]})}),makeQuery(id+"F3.boolean.opBoolean","COPY",FACE,{"derivedFrom":makeQuery(id+"F3.opExtrude","SWEPT_FACE",FACE,{"disambiguationData":[OSD([subQ0]),TDD([makeQuery(id+"F2.imprint","IMPRINT",EDGE,{"disambiguationData":[TD([[makeQuery(id+"F2.imprint","INTERSECT",VERTEX,{"derivedFrom":[subQ0,sQuery(id+"F2.wireOp",EDGE,"E4.right"),sQuery(id+"F2.wireOp",EDGE,"E16")]}),1.0]])],"derivedFrom":subQ0})])]})}),makeQuery(id+"F3.boolean.opBoolean","COPY",FACE,{"derivedFrom":makeQuery(id+"F3.opExtrude","SWEPT_FACE",FACE,{"disambiguationData":[OSD([sQuery(id+"F2.wireOp",EDGE,"E61")])]})}),makeQuery(id+"F3.boolean.opBoolean","COPY",FACE,{"derivedFrom":makeQuery(id+"F3.opExtrude","SWEPT_FACE",FACE,{"disambiguationData":[OSD([sQuery(id+"F2.wireOp",EDGE,"E64.MirrorCS")])]})})],"fromTools":[makeQuery(id+"F5.opExtrude","SWEPT_FACE",FACE,{"disambiguationData":[OSD([sQuery(id+"F4.wireOp",EDGE,"E65.bottom")])]})]}),makeQuery(id+"F9.opExtrude","SWEPT_FACE",FACE,{"disambiguationData":[OSD([sQuery(id+"F8.wireOp",EDGE,"E71.top")])]}),makeQuery(id+"F9.opExtrude","SWEPT_FACE",FACE,{"disambiguationData":[OSD([sQuery(id+"F8.wireOp",EDGE,"E73.MirrorCS")])]})]});}
            var sketch = newSketch(context, id + "F10", { "sketchPlane" : qUnion([Q0])});
            skLineSegment(sketch, "E76.bottom", {"start": v(38.1, -95.19) * mm, "end": v(34.92, -95.19) * mm});
            skLineSegment(sketch, "E76.top", {"start": v(38.1, 95.19) * mm, "end": v(34.92, 95.19) * mm});
            skLineSegment(sketch, "E76.left", {"start": v(38.1, -95.19) * mm, "end": v(38.1, 95.19) * mm});
            skLineSegment(sketch, "E76.right", {"start": v(34.92, -95.19) * mm, "end": v(34.92, 95.19) * mm});
            skLineSegment(sketch, "E77.MirrorCS", {"start": v(-38.1, -95.19) * mm, "end": v(-34.92, -95.19) * mm});
            skLineSegment(sketch, "E78.MirrorCS", {"start": v(-34.92, -95.19) * mm, "end": v(-34.92, 95.19) * mm});
            skLineSegment(sketch, "E79.MirrorCS", {"start": v(-38.1, -95.19) * mm, "end": v(-38.1, 95.19) * mm});
            skLineSegment(sketch, "E80.MirrorCS", {"start": v(-38.1, 95.19) * mm, "end": v(-34.92, 95.19) * mm});
            skSolve(sketch);
        }
        {
            var Q0;
            Q0=qSketchRegion(id+"F10",true);
            extrude(context, id + "F11", {"entities" : qUnion([Q0]), "operationType" : NewBodyOperationType.ADD, "depth" : 3.17 * mm, "offsetDistance" : 25.4 * mm});
        }
    });
